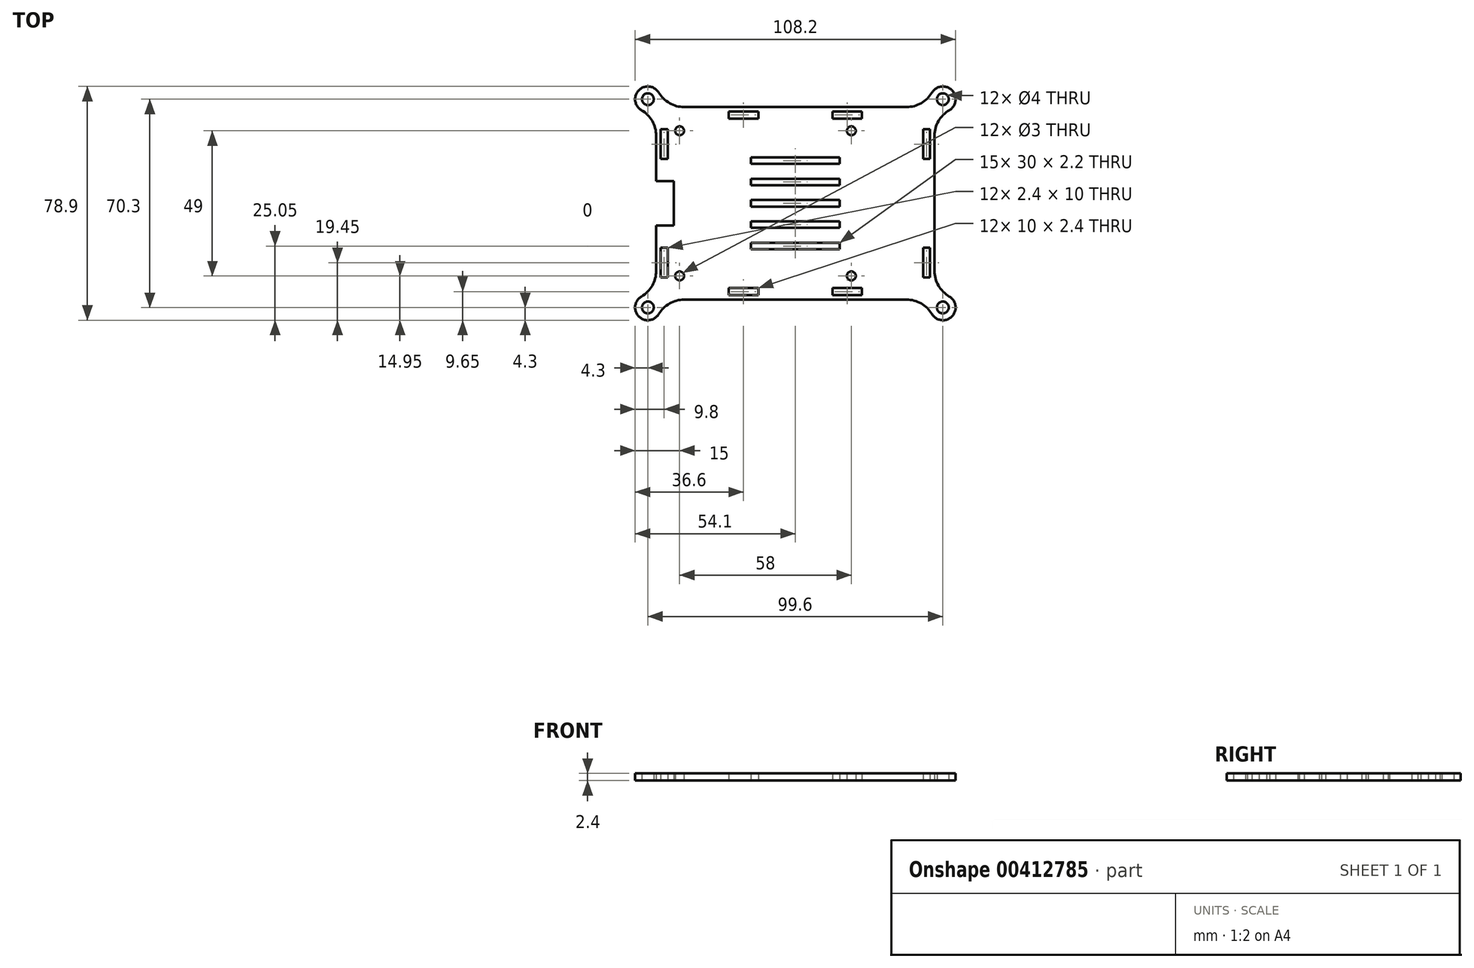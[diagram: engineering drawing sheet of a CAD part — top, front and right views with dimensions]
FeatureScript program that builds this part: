
annotation { "Feature Type Name" : "Feature", "Feature Type Description" : "" }
export const myFeature = defineFeature(function(context is Context, id is Id, definition is map)
    precondition{}
    {
        {
            var Q0;
            Q0=qCreatedBy(makeId("Top.planeOp"),FACE);
            var sketch = newSketch(context, id + "F0", { "sketchPlane" : qUnion([Q0])});
            skLineSegment(sketch, "E0.bottom", {"start": v(37.53, 32.5) * mm, "end": v(-37.53, 32.5) * mm});
            skLineSegment(sketch, "E0.top", {"start": v(37.53, -32.5) * mm, "end": v(-37.53, -32.5) * mm});
            skLineSegment(sketch, "E0.left", {"start": v(47, 22.8) * mm, "end": v(47, -22.8) * mm});
            skLineSegment(sketch, "E0.right", {"start": v(-47, 22.8) * mm, "end": v(-47, 7.5) * mm});
            skPoint(sketch, "E0.middle", {"position": v(0, 0) * mm});
            skCircle(sketch, "E1", {"center": v(-49.8, 35.15) * mm, "radius": 2 * mm});
            skArc(sketch, "E2", {"start": v(-46.11, 37.36) * mm, "mid": v(-52.86, 38.17) * mm, "end": v(-51.97, 31.43) * mm});
            skCircle(sketch, "E3", {"center": v(49.8, 35.15) * mm, "radius": 2 * mm});
            skArc(sketch, "E4", {"start": v(51.97, 31.43) * mm, "mid": v(52.86, 38.17) * mm, "end": v(46.11, 37.36) * mm});
            skCircle(sketch, "E5", {"center": v(49.8, -35.15) * mm, "radius": 2 * mm});
            skArc(sketch, "E6", {"start": v(46.11, -37.36) * mm, "mid": v(52.86, -38.17) * mm, "end": v(51.97, -31.43) * mm});
            skCircle(sketch, "E7", {"center": v(-49.8, -35.15) * mm, "radius": 2 * mm});
            skArc(sketch, "E8", {"start": v(-51.97, -31.43) * mm, "mid": v(-52.86, -38.17) * mm, "end": v(-46.11, -37.36) * mm});
            skPoint(sketch, "E9.orphan", {"position": v(-47, 32.5) * mm});
            skPoint(sketch, "E10.visualSharp", {"position": v(-46.41, 32.5) * mm});
            skArc(sketch, "E10.filletArc", {"start": v(-46.11, 37.36) * mm, "mid": v(-42.46, 33.8) * mm, "end": v(-37.53, 32.5) * mm});
            skPoint(sketch, "E11.visualSharp", {"position": v(-47, 31.89) * mm});
            skArc(sketch, "E11.filletArc", {"start": v(-47, 22.8) * mm, "mid": v(-48.33, 27.78) * mm, "end": v(-51.97, 31.43) * mm});
            skPoint(sketch, "E12.orphan", {"position": v(47, 32.5) * mm});
            skPoint(sketch, "E13.orphan", {"position": v(47, -32.5) * mm});
            skPoint(sketch, "E14.orphan", {"position": v(-47, -32.5) * mm});
            skPoint(sketch, "E15.visualSharp", {"position": v(-46.41, -32.5) * mm});
            skArc(sketch, "E15.filletArc", {"start": v(-37.53, -32.5) * mm, "mid": v(-42.46, -33.8) * mm, "end": v(-46.11, -37.36) * mm});
            skPoint(sketch, "E16.visualSharp", {"position": v(-47, -31.89) * mm});
            skArc(sketch, "E16.filletArc", {"start": v(-51.97, -31.43) * mm, "mid": v(-48.33, -27.78) * mm, "end": v(-47, -22.8) * mm});
            skPoint(sketch, "E17.visualSharp", {"position": v(46.41, -32.5) * mm});
            skArc(sketch, "E17.filletArc", {"start": v(46.11, -37.36) * mm, "mid": v(42.46, -33.8) * mm, "end": v(37.53, -32.5) * mm});
            skPoint(sketch, "E18.visualSharp", {"position": v(47, -31.89) * mm});
            skArc(sketch, "E18.filletArc", {"start": v(47, -22.8) * mm, "mid": v(48.33, -27.78) * mm, "end": v(51.97, -31.43) * mm});
            skPoint(sketch, "E19.visualSharp", {"position": v(47, 31.89) * mm});
            skArc(sketch, "E19.filletArc", {"start": v(51.97, 31.43) * mm, "mid": v(48.33, 27.78) * mm, "end": v(47, 22.8) * mm});
            skPoint(sketch, "E20.visualSharp", {"position": v(46.41, 32.5) * mm});
            skArc(sketch, "E20.filletArc", {"start": v(37.53, 32.5) * mm, "mid": v(42.46, 33.8) * mm, "end": v(46.11, 37.36) * mm});
            skCircle(sketch, "E21", {"center": v(-39.1, 24.5) * mm, "radius": 1.5 * mm});
            skCircle(sketch, "E22", {"center": v(18.9, 24.5) * mm, "radius": 1.5 * mm});
            skCircle(sketch, "E23", {"center": v(-39.1, -24.5) * mm, "radius": 1.5 * mm});
            skCircle(sketch, "E24", {"center": v(18.9, -24.5) * mm, "radius": 1.5 * mm});
            skLineSegment(sketch, "E25.bottom", {"start": v(-41, 7.5) * mm, "end": v(-47, 7.5) * mm});
            skLineSegment(sketch, "E25.top", {"start": v(-41, -7.5) * mm, "end": v(-47, -7.5) * mm});
            skLineSegment(sketch, "E25.left", {"start": v(-41, 7.5) * mm, "end": v(-41, -7.5) * mm});
            skPoint(sketch, "E25.middle", {"position": v(-47, 0) * mm});
            skPoint(sketch, "E25.right.start.orphan", {"position": v(-53, 7.5) * mm});
            skPoint(sketch, "E26.orphan", {"position": v(-53, -7.5) * mm});
            skLineSegment(sketch, "E27.trimOffspring", {"start": v(-47, -7.5) * mm, "end": v(-47, -22.8) * mm});
            skLineSegment(sketch, "E28.bottom", {"start": v(15, 1.1) * mm, "end": v(-15, 1.1) * mm});
            skLineSegment(sketch, "E28.top", {"start": v(15, -1.1) * mm, "end": v(-15, -1.1) * mm});
            skLineSegment(sketch, "E28.left", {"start": v(15, 1.1) * mm, "end": v(15, -1.1) * mm});
            skLineSegment(sketch, "E28.right", {"start": v(-15, 1.1) * mm, "end": v(-15, -1.1) * mm});
            skPoint(sketch, "E29.middle", {"position": v(0, 7.2) * mm});
            skLineSegment(sketch, "E30.bottom", {"start": v(15, 8.3) * mm, "end": v(-15, 8.3) * mm});
            skLineSegment(sketch, "E30.top", {"start": v(15, 6.1) * mm, "end": v(-15, 6.1) * mm});
            skLineSegment(sketch, "E30.left", {"start": v(15, 8.3) * mm, "end": v(15, 6.1) * mm});
            skLineSegment(sketch, "E30.right", {"start": v(-15, 8.3) * mm, "end": v(-15, 6.1) * mm});
            skPoint(sketch, "E31.middle", {"position": v(0, 14.4) * mm});
            skLineSegment(sketch, "E32.bottom", {"start": v(15, 15.5) * mm, "end": v(-15, 15.5) * mm});
            skLineSegment(sketch, "E32.top", {"start": v(15, 13.3) * mm, "end": v(-15, 13.3) * mm});
            skLineSegment(sketch, "E32.left", {"start": v(15, 15.5) * mm, "end": v(15, 13.3) * mm});
            skLineSegment(sketch, "E32.right", {"start": v(-15, 15.5) * mm, "end": v(-15, 13.3) * mm});
            skPoint(sketch, "E33.middle", {"position": v(0, -7.2) * mm});
            skLineSegment(sketch, "E34.bottom", {"start": v(15, -6.1) * mm, "end": v(-15, -6.1) * mm});
            skLineSegment(sketch, "E34.top", {"start": v(15, -8.3) * mm, "end": v(-15, -8.3) * mm});
            skLineSegment(sketch, "E34.left", {"start": v(15, -6.1) * mm, "end": v(15, -8.3) * mm});
            skLineSegment(sketch, "E34.right", {"start": v(-15, -6.1) * mm, "end": v(-15, -8.3) * mm});
            skPoint(sketch, "E35.middle", {"position": v(0, -14.4) * mm});
            skLineSegment(sketch, "E36.bottom", {"start": v(15, -13.3) * mm, "end": v(-15, -13.3) * mm});
            skLineSegment(sketch, "E36.top", {"start": v(15, -15.5) * mm, "end": v(-15, -15.5) * mm});
            skLineSegment(sketch, "E36.left", {"start": v(15, -13.3) * mm, "end": v(15, -15.5) * mm});
            skLineSegment(sketch, "E36.right", {"start": v(-15, -13.3) * mm, "end": v(-15, -15.5) * mm});
            skLineSegment(sketch, "E37.bottom", {"start": v(-22.5, 31) * mm, "end": v(-12.5, 31) * mm});
            skLineSegment(sketch, "E37.top", {"start": v(-22.5, 28.6) * mm, "end": v(-12.5, 28.6) * mm});
            skLineSegment(sketch, "E37.left", {"start": v(-22.5, 31) * mm, "end": v(-22.5, 28.6) * mm});
            skLineSegment(sketch, "E37.right", {"start": v(-12.5, 31) * mm, "end": v(-12.5, 28.6) * mm});
            skLineSegment(sketch, "E38.bottom", {"start": v(12.5, 31) * mm, "end": v(22.5, 31) * mm});
            skLineSegment(sketch, "E38.top", {"start": v(12.5, 28.6) * mm, "end": v(22.5, 28.6) * mm});
            skLineSegment(sketch, "E38.left", {"start": v(12.5, 31) * mm, "end": v(12.5, 28.6) * mm});
            skLineSegment(sketch, "E38.right", {"start": v(22.5, 31) * mm, "end": v(22.5, 28.6) * mm});
            skLineSegment(sketch, "E39.bottom", {"start": v(43.1, 25) * mm, "end": v(45.5, 25) * mm});
            skLineSegment(sketch, "E39.top", {"start": v(43.1, 15) * mm, "end": v(45.5, 15) * mm});
            skLineSegment(sketch, "E39.left", {"start": v(43.1, 25) * mm, "end": v(43.1, 15) * mm});
            skLineSegment(sketch, "E39.right", {"start": v(45.5, 25) * mm, "end": v(45.5, 15) * mm});
            skLineSegment(sketch, "E40.bottom", {"start": v(43.1, -15) * mm, "end": v(45.5, -15) * mm});
            skLineSegment(sketch, "E40.top", {"start": v(43.1, -25) * mm, "end": v(45.5, -25) * mm});
            skLineSegment(sketch, "E40.left", {"start": v(43.1, -15) * mm, "end": v(43.1, -25) * mm});
            skLineSegment(sketch, "E40.right", {"start": v(45.5, -15) * mm, "end": v(45.5, -25) * mm});
            skLineSegment(sketch, "E41.bottom", {"start": v(12.5, -28.6) * mm, "end": v(22.5, -28.6) * mm});
            skLineSegment(sketch, "E41.top", {"start": v(12.5, -31) * mm, "end": v(22.5, -31) * mm});
            skLineSegment(sketch, "E41.left", {"start": v(12.5, -28.6) * mm, "end": v(12.5, -31) * mm});
            skLineSegment(sketch, "E41.right", {"start": v(22.5, -28.6) * mm, "end": v(22.5, -31) * mm});
            skLineSegment(sketch, "E42.bottom", {"start": v(-22.5, -28.6) * mm, "end": v(-12.5, -28.6) * mm});
            skLineSegment(sketch, "E42.top", {"start": v(-22.5, -31) * mm, "end": v(-12.5, -31) * mm});
            skLineSegment(sketch, "E42.left", {"start": v(-22.5, -28.6) * mm, "end": v(-22.5, -31) * mm});
            skLineSegment(sketch, "E42.right", {"start": v(-12.5, -28.6) * mm, "end": v(-12.5, -31) * mm});
            skLineSegment(sketch, "E43.bottom", {"start": v(-45.5, 25) * mm, "end": v(-43.1, 25) * mm});
            skLineSegment(sketch, "E43.top", {"start": v(-45.5, 15) * mm, "end": v(-43.1, 15) * mm});
            skLineSegment(sketch, "E43.left", {"start": v(-45.5, 25) * mm, "end": v(-45.5, 15) * mm});
            skLineSegment(sketch, "E43.right", {"start": v(-43.1, 25) * mm, "end": v(-43.1, 15) * mm});
            skPoint(sketch, "E44.oppositeSnap0", {"position": v(-43.1, 20) * mm});
            skLineSegment(sketch, "E44.bottom", {"start": v(-45.5, -15) * mm, "end": v(-43.1, -15) * mm});
            skLineSegment(sketch, "E44.top", {"start": v(-45.5, -25) * mm, "end": v(-43.1, -25) * mm});
            skLineSegment(sketch, "E44.left", {"start": v(-45.5, -15) * mm, "end": v(-45.5, -25) * mm});
            skLineSegment(sketch, "E44.right", {"start": v(-43.1, -15) * mm, "end": v(-43.1, -25) * mm});
            skSolve(sketch);
        }
        {
            var Q0;
            Q0=qSketchRegion(id+"F0",true);
            extrude(context, id + "F1", {"entities" : qUnion([Q0]), "depth" : 2.4 * mm});
        }
    });
